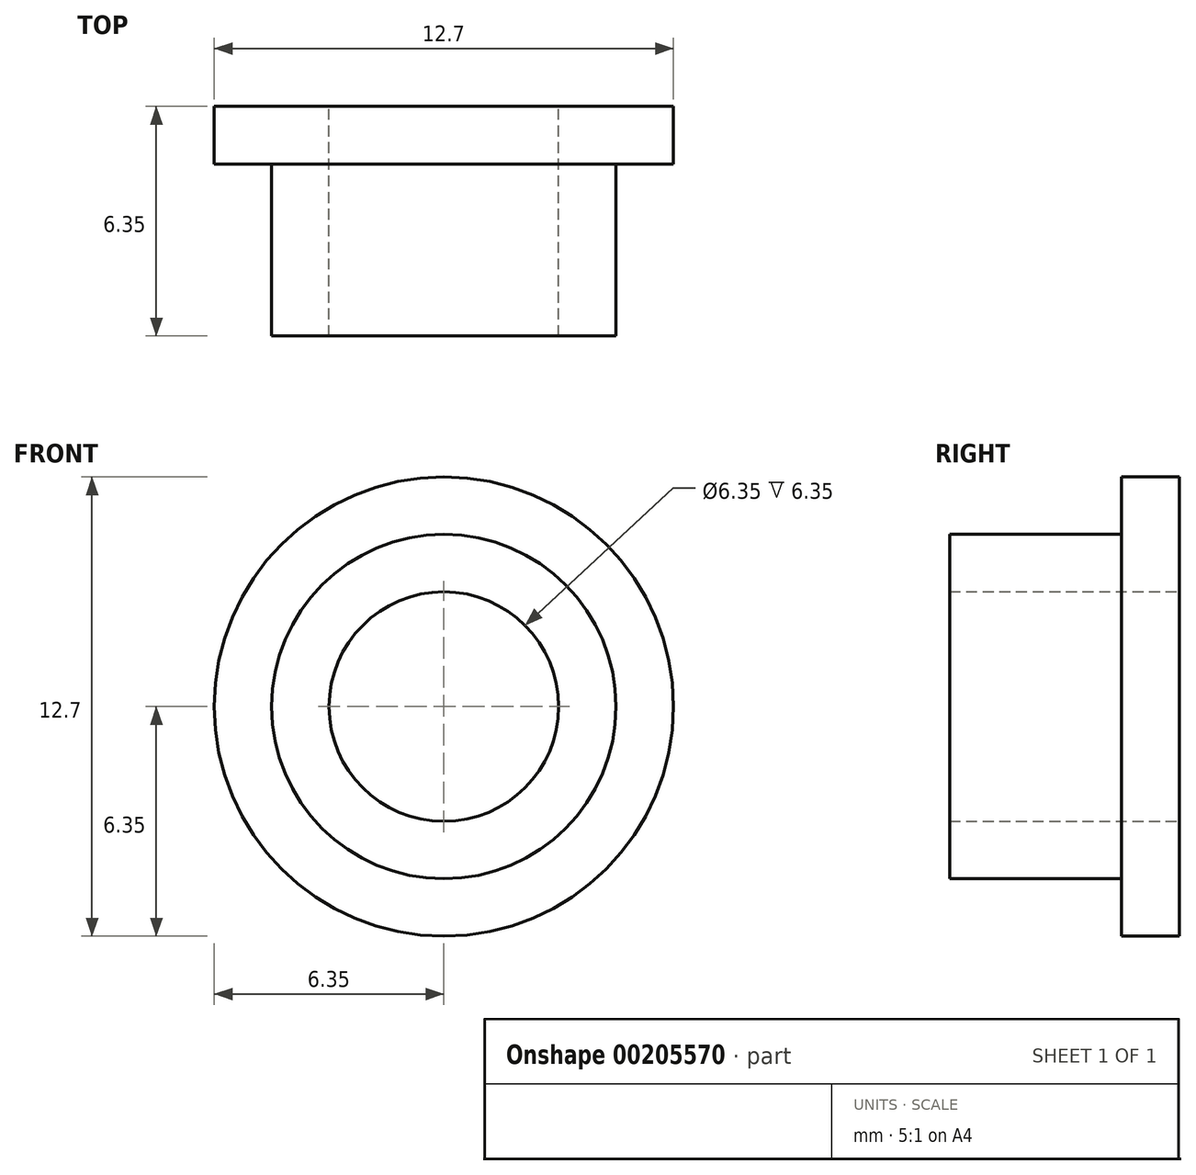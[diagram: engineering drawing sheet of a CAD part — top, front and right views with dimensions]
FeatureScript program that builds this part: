
annotation { "Feature Type Name" : "Feature", "Feature Type Description" : "" }
export const myFeature = defineFeature(function(context is Context, id is Id, definition is map)
    precondition{}
    {
        {
            var Q0;
            Q0=qCreatedBy(makeId("Front.planeOp"),FACE);
            var sketch = newSketch(context, id + "F0", { "sketchPlane" : qUnion([Q0])});
            skCircle(sketch, "E0", {"center": v(0, 0) * mm, "radius": 6.35 * mm});
            skSolve(sketch);
        }
        {
            var Q0;
            Q0=qSketchRegion(id+"F0",true);
            extrude(context, id + "F1", {"entities" : qUnion([Q0]), "flatOperationType" : FlatOperationType.REMOVE, "oppositeDirection" : true, "offsetDistance" : 25.4 * mm, "depth" : 1.6 * mm, "domain" : OperationDomain.MODEL});
        }
        {
            var Q0;
            Q0=makeQuery(id+"F1.opExtrude","CAP_FACE",FACE,{"disambiguationData":[OSD([sQuery(id+"F0.wireOp",EDGE,"E0")])],"isStart":true});
            var sketch = newSketch(context, id + "F2", { "sketchPlane" : qUnion([Q0])});
            skCircle(sketch, "E1", {"center": v(0, 0) * mm, "radius": 4.76 * mm});
            skSolve(sketch);
        }
        {
            var Q0;
            Q0=qSketchRegion(id+"F2",true);
            extrude(context, id + "F3", {"entities" : qUnion([Q0]), "operationType" : NewBodyOperationType.ADD, "flatOperationType" : FlatOperationType.REMOVE, "offsetDistance" : 25.4 * mm, "depth" : 4.75 * mm, "domain" : OperationDomain.MODEL});
        }
        {
            var Q0;
            Q0=makeQuery(id+"F1.opExtrude","CAP_FACE",FACE,{"disambiguationData":[OSD([sQuery(id+"F0.wireOp",EDGE,"E0")])],"isStart":true});
            var sketch = newSketch(context, id + "F4", { "sketchPlane" : qUnion([Q0])});
            skCircle(sketch, "E2", {"center": v(0, 0) * mm, "radius": 3.18 * mm});
            skSolve(sketch);
        }
        {
            var Q0;
            Q0=qSketchRegion(id+"F4",true);
            extrude(context, id + "F5", {"entities" : qUnion([Q0]), "operationType" : NewBodyOperationType.REMOVE, "depth" : 25.4 * mm, "symmetric" : true});
        }
    });
